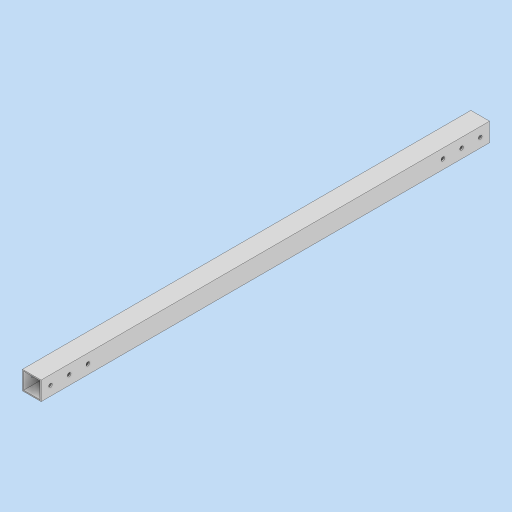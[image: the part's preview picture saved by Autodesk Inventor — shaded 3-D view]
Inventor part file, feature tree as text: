
AUTODESK INVENTOR PART (.ipt)
format: ipt  version: 2024 (Build 280153000, 153)  size: 115,200 bytes
history: native  units: in
note: dims shown in document units (in); Inventor stores cm internally (conversion verified against a paired STEP export)
features: extrude x2, sketch x2, projected_geometry x1
ambient origin geometry x8: Origin, YZ Plane, XZ Plane, XY Plane, X Axis, Y Axis, Z Axis, Center Point
bodies: Solid1 (feature_tree)
feature tree (5):
  extrude  "Extrusion1"  Depth=1.0in
  extrude  "Extrusion2"  Depth=24.0in TaperAngle=0.0deg
  sketch  "Sketch1"  dims[d0=1.0in d1=1.0in]
  sketch  "Sketch2"  dims[d2=0.0625in d3=24.0in d4=0.0in d5=0.203in d7=0.5in d8=1.0in d9=1.0in d10=0.0in d11=0.0in]
  projected_geometry  "Projected Loop1"
